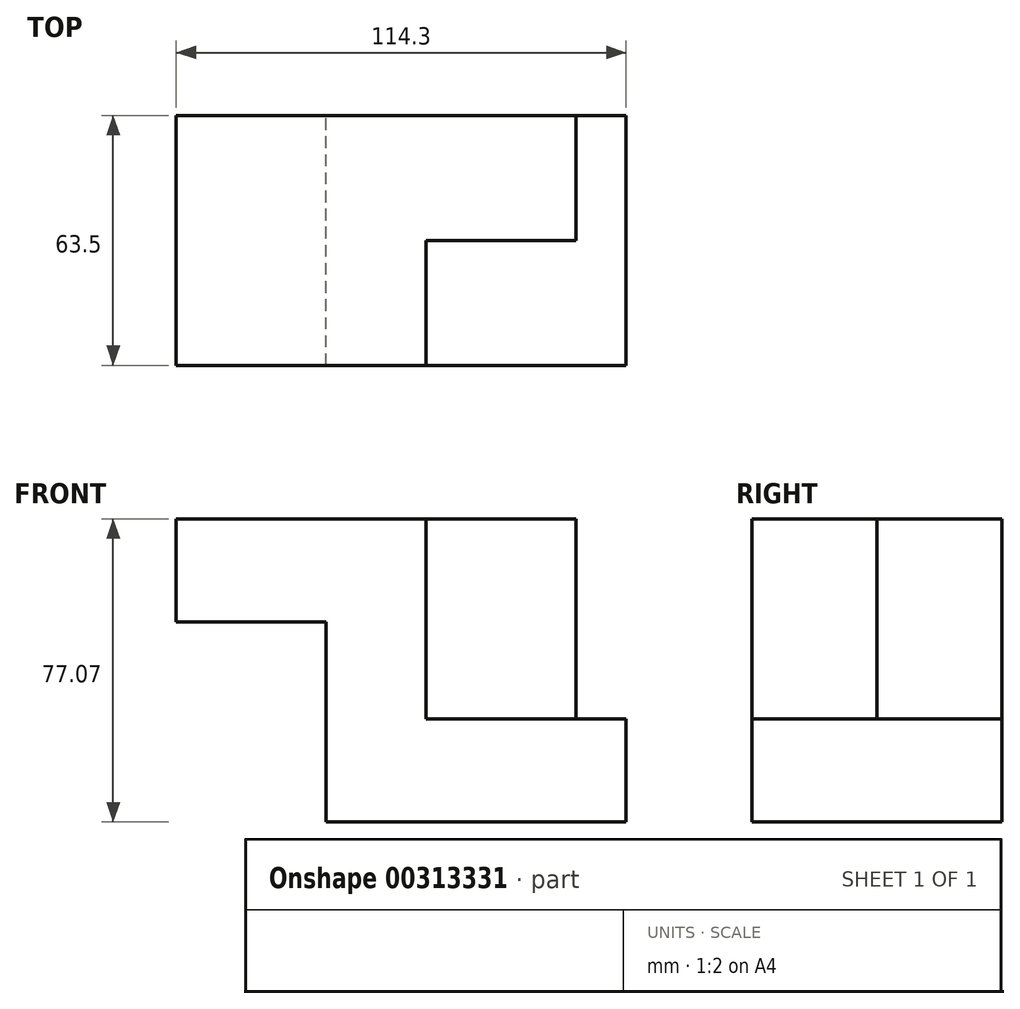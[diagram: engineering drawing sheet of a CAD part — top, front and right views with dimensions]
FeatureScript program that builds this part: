
annotation { "Feature Type Name" : "Feature", "Feature Type Description" : "" }
export const myFeature = defineFeature(function(context is Context, id is Id, definition is map)
    precondition{}
    {
        {
            var Q0;
            Q0=qCreatedBy(makeId("Front.planeOp"),FACE);
            var sketch = newSketch(context, id + "F0", { "sketchPlane" : qUnion([Q0])});
            skLineSegment(sketch, "E0", {"start": v(-45.47, -48.44) * mm, "end": v(30.73, -48.44) * mm});
            skLineSegment(sketch, "E1", {"start": v(-45.47, -48.44) * mm, "end": v(-45.47, 2.36) * mm});
            skLineSegment(sketch, "E2", {"start": v(-45.47, 2.36) * mm, "end": v(-83.57, 2.36) * mm});
            skLineSegment(sketch, "E3", {"start": v(-83.57, 2.36) * mm, "end": v(-83.57, 28.63) * mm});
            skLineSegment(sketch, "E4", {"start": v(-83.57, 28.63) * mm, "end": v(-20.07, 28.63) * mm});
            skLineSegment(sketch, "E5", {"start": v(-20.07, 28.63) * mm, "end": v(-20.07, -22.17) * mm});
            skLineSegment(sketch, "E6", {"start": v(-20.07, -22.17) * mm, "end": v(30.73, -22.17) * mm});
            skLineSegment(sketch, "E7", {"start": v(30.73, -22.17) * mm, "end": v(30.73, -48.44) * mm});
            skSolve(sketch);
        }
        {
            var Q0;
            Q0=makeQuery(id+"F0.imprint","IMPRINT",FACE,{"disambiguationData":[TD([[makeQuery(id+"F0.imprint","IMPRINT",EDGE,{"derivedFrom":sQuery(id+"F0.wireOp",EDGE,"E0")}),1.0]])]});
            extrude(context, id + "F1", {"entities" : qUnion([Q0]), "depth" : 63.5 * mm});
        }
        {
            var Q0;
            Q0=makeQuery(id+"F1.opExtrude","SWEPT_FACE",FACE,{"disambiguationData":[OSD([sQuery(id+"F0.wireOp",EDGE,"E5")])]});
            var sketch = newSketch(context, id + "F2", { "sketchPlane" : qUnion([Q0])});
            skLineSegment(sketch, "E8", {"start": v(0, 28.63) * mm, "end": v(-31.75, 28.63) * mm});
            skLineSegment(sketch, "E9", {"start": v(-31.75, 28.63) * mm, "end": v(-31.75, -22.17) * mm});
            skLineSegment(sketch, "E10", {"start": v(-31.75, -22.17) * mm, "end": v(0, -22.17) * mm});
            skLineSegment(sketch, "E11", {"start": v(0, -22.17) * mm, "end": v(0, 28.63) * mm});
            skSolve(sketch);
        }
        {
            var Q0;
            Q0=makeQuery(id+"F2.imprint","IMPRINT",FACE,{"disambiguationData":[TD([[makeQuery(id+"F2.imprint","IMPRINT",EDGE,{"derivedFrom":sQuery(id+"F2.wireOp",EDGE,"E8")}),-1.0]])]});
            extrude(context, id + "F3", {"entities" : qUnion([Q0]), "operationType" : NewBodyOperationType.ADD, "depth" : 38.1 * mm});
        }
    });
